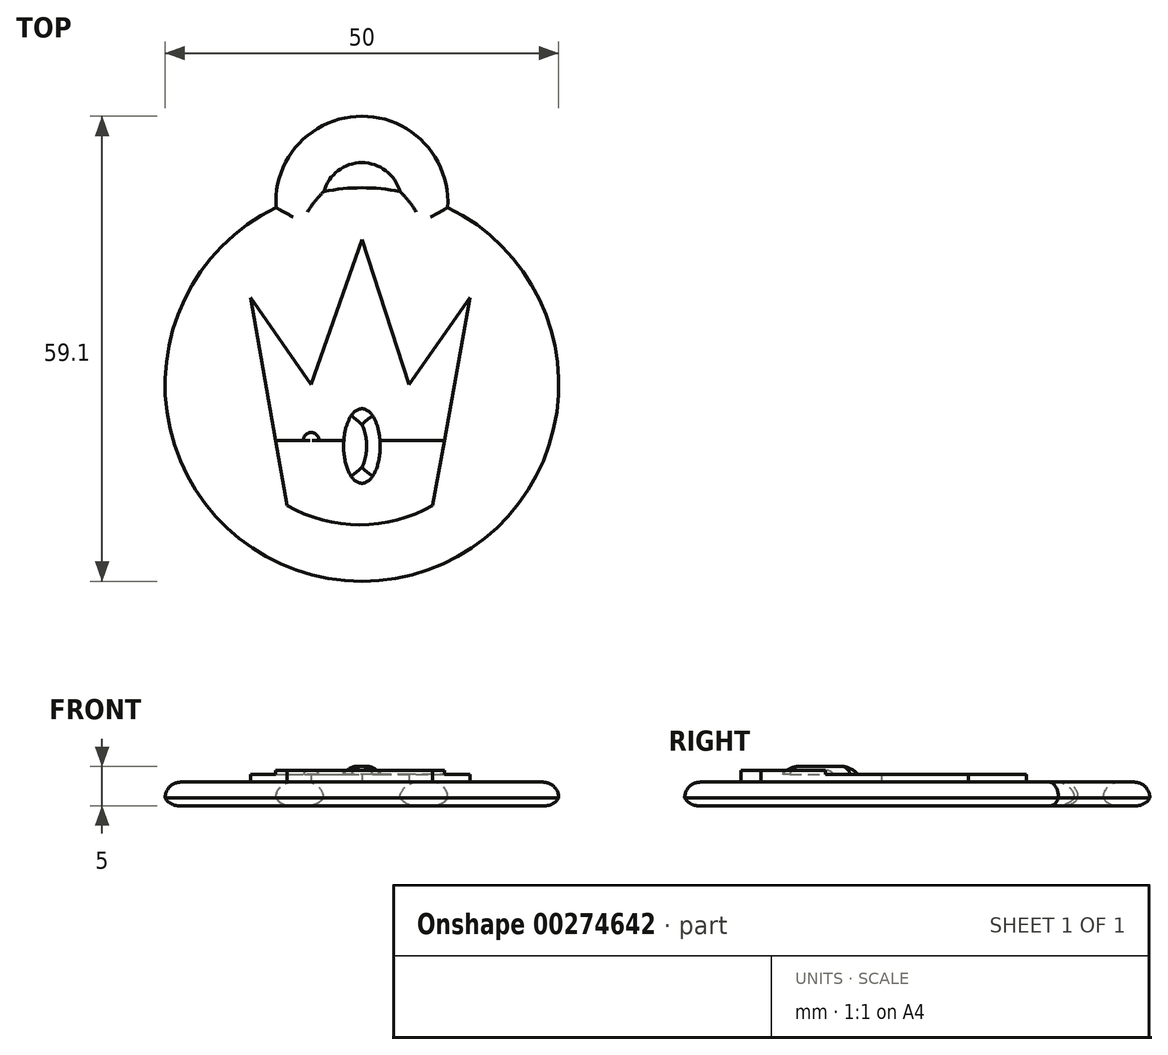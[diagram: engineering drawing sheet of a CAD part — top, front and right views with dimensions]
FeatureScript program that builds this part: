
annotation { "Feature Type Name" : "Feature", "Feature Type Description" : "" }
export const myFeature = defineFeature(function(context is Context, id is Id, definition is map)
    precondition{}
    {
        {
            var Q0;
            Q0=qCreatedBy(makeId("Top.planeOp"),FACE);
            var sketch = newSketch(context, id + "F0", { "sketchPlane" : qUnion([Q0])});
            skCircle(sketch, "E0", {"center": v(0, 0) * mm, "radius": 25 * mm});
            skSolve(sketch);
        }
        {
            var Q0;
            Q0=qCreatedBy(makeId("Top.planeOp"),FACE);
            var sketch = newSketch(context, id + "F1", { "sketchPlane" : qUnion([Q0])});
            skCircle(sketch, "E1", {"center": v(0, 23.17) * mm, "radius": 10.93 * mm});
            skCircle(sketch, "E2", {"center": v(0, 23.17) * mm, "radius": 5.01 * mm});
            skSolve(sketch);
        }
        {
            var Q0;
            Q0=makeQuery(id+"F0.imprint","IMPRINT",FACE,{"disambiguationData":[TD([[makeQuery(id+"F0.imprint","IMPRINT",EDGE,{"derivedFrom":sQuery(id+"F0.wireOp",EDGE,"E0")}),1.0]])]});
            var Q1;
            Q1=makeQuery(id+"F1.imprint","IMPRINT",FACE,{"disambiguationData":[TD([[makeQuery(id+"F1.imprint","IMPRINT",EDGE,{"derivedFrom":sQuery(id+"F1.wireOp",EDGE,"E1")}),1.0]])]});
            extrude(context, id + "F2", {"entities" : qUnion([Q0, Q1]), "depth" : 3 * mm});
        }
        {
            var Q0;
            Q0=makeQuery(id+"F2.opExtrude","CAP_FACE",FACE,{"disambiguationData":[OSD([sQuery(id+"F0.wireOp",EDGE,"E0")])],"isStart":false});
            var sketch = newSketch(context, id + "F3", { "sketchPlane" : qUnion([Q0])});
            skLineSegment(sketch, "E3", {"start": v(0, 18.31) * mm, "end": v(0, -16.1) * mm});
            skLineSegment(sketch, "E4", {"start": v(-13.94, 11.03) * mm, "end": v(13.74, 11.03) * mm});
            skSolve(sketch);
        }
        {
            var Q0;
            Q0=makeQuery(id+"F3.imprint","IMPRINT",FACE,{"disambiguationData":[TD([[makeQuery(id+"F3.imprint","IMPRINT",EDGE,{"derivedFrom":makeQuery(id+"F2.opExtrude","CAP_EDGE",EDGE,{"disambiguationData":[OSD([sQuery(id+"F0.wireOp",EDGE,"E0")])],"isStart":false})}),1.0]])]});
            var sketch = newSketch(context, id + "F4", { "sketchPlane" : qUnion([Q0])});
            skLineSegment(sketch, "E5", {"start": v(-14.16, 11.03) * mm, "end": v(-9.53, -15.33) * mm});
            skLineSegment(sketch, "E6", {"start": v(13.74, 11.03) * mm, "end": v(9, -15.33) * mm});
            skLineSegment(sketch, "E7", {"start": v(-14.16, 11.03) * mm, "end": v(-6.44, 0) * mm});
            skLineSegment(sketch, "E8", {"start": v(13.74, 11.03) * mm, "end": v(6.02, 0) * mm});
            skLineSegment(sketch, "E9", {"start": v(-6.44, 0) * mm, "end": v(0, 18.42) * mm});
            skLineSegment(sketch, "E10", {"start": v(6.02, 0) * mm, "end": v(0, 18.42) * mm});
            skArc(sketch, "E11", {"start": v(-9.53, -15.33) * mm, "mid": v(-0.27, -17.83) * mm, "end": v(9, -15.33) * mm});
            skSolve(sketch);
        }
        {
            var Q0;
            Q0 = qSketchRegion(id + "F4", true);
            extrude(context, id + "F5", {"entities" : qUnion([Q0]), "depth" : 1 * mm});
        }
        {
            var Q0;
            Q0=makeQuery(id+"F5.opExtrude","CAP_FACE",FACE,{"disambiguationData":[OSD([sQuery(id+"F4.wireOp",EDGE,"E5"),sQuery(id+"F4.wireOp",EDGE,"E6"),sQuery(id+"F4.wireOp",EDGE,"E7"),sQuery(id+"F4.wireOp",EDGE,"E8"),sQuery(id+"F4.wireOp",EDGE,"E9"),sQuery(id+"F4.wireOp",EDGE,"E10"),sQuery(id+"F4.wireOp",EDGE,"E11")])],"isStart":false});
            var sketch = newSketch(context, id + "F6", { "sketchPlane" : qUnion([Q0])});
            skEllipse(sketch, "E12", {"center": v(0, -7.8) * mm, "majorRadius": 4.74 * mm, "minorRadius": 2.32 * mm, "majorAxis": v(0, -1)});
            skSolve(sketch);
        }
        {
            var Q0;
            Q0=makeQuery(id+"F6.imprint","IMPRINT",FACE,{"disambiguationData":[TD([[makeQuery(id+"F6.imprint","IMPRINT",EDGE,{"derivedFrom":sQuery(id+"F6.wireOp",EDGE,"E12")}),1.0]])]});
            extrude(context, id + "F7", {"entities" : qUnion([Q0]), "operationType" : NewBodyOperationType.ADD, "depth" : 1 * mm});
        }
        {
            var Q0;
            Q0=makeQuery(id+"F7.opExtrude","CAP_EDGE",EDGE,{"disambiguationData":[OSD([sQuery(id+"F6.wireOp",EDGE,"E12")])],"isStart":false});
            fillet(context, id + "F8", {"entities" : qUnion([Q0]), "radius" : 2 * mm, "tangentPropagation" : true, "allowEdgeOverflow" : false});
        }
        {
            var Q0;
            Q0=makeQuery(id+"F2.opExtrude","SWEPT_BODY",BODY,{"disambiguationData":[OSD([sQuery(id+"F0.wireOp",EDGE,"E0")])]});
            var Q1;
            Q1=makeQuery(id+"F2.opExtrude","SWEPT_BODY",BODY,{"disambiguationData":[OSD([sQuery(id+"F1.wireOp",EDGE,"E1"),sQuery(id+"F1.wireOp",EDGE,"E2")])]});
            var Q2;
            Q2=makeQuery(id+"F5.opExtrude","SWEPT_BODY",BODY,{"disambiguationData":[OSD([sQuery(id+"F4.wireOp",EDGE,"E5"),sQuery(id+"F4.wireOp",EDGE,"E6"),sQuery(id+"F4.wireOp",EDGE,"E7"),sQuery(id+"F4.wireOp",EDGE,"E8"),sQuery(id+"F4.wireOp",EDGE,"E9"),sQuery(id+"F4.wireOp",EDGE,"E10"),sQuery(id+"F4.wireOp",EDGE,"E11")])]});
            booleanBodies(context, id + "F9", {"operationType" : BooleanOperationType.UNION, "tools" : qUnion([Q0, Q1, Q2])});
        }
        {
            var Q0;
            {var subQ0=sQuery(id+"F0.wireOp",EDGE,"E0");var subQ1=sQuery(id+"F1.wireOp",EDGE,"E1");Q0=makeQuery(id+"F9.opBoolean","SPLIT",EDGE,{"disambiguationData":[TD([makeQuery(id+"F2.opExtrude","SWEPT_FACE",FACE,{"disambiguationData":[OSD([subQ1])]})])],"derivedFrom":makeQuery(id+"F2.opExtrude","CAP_EDGE",EDGE,{"disambiguationData":[OSD([subQ0])],"isStart":false})});}
            var Q1;
            Q1=makeQuery(id+"F2.opExtrude","CAP_EDGE",EDGE,{"disambiguationData":[OSD([sQuery(id+"F1.wireOp",EDGE,"E1")])],"isStart":false});
            var Q2;
            {var subQ0=sQuery(id+"F0.wireOp",EDGE,"E0");var subQ1=sQuery(id+"F1.wireOp",EDGE,"E2");Q2=makeQuery(id+"F9.opBoolean","SPLIT",EDGE,{"disambiguationData":[TD([makeQuery(id+"F2.opExtrude","SWEPT_FACE",FACE,{"disambiguationData":[OSD([subQ1])]})])],"derivedFrom":makeQuery(id+"F2.opExtrude","CAP_EDGE",EDGE,{"disambiguationData":[OSD([subQ0])],"isStart":false})});}
            var Q3;
            Q3=makeQuery(id+"F2.opExtrude","CAP_EDGE",EDGE,{"disambiguationData":[OSD([sQuery(id+"F1.wireOp",EDGE,"E2")])],"isStart":false});
            fillet(context, id + "F10", {"entities" : qUnion([Q0, Q1, Q2, Q3]), "radius" : 2 * mm, "tangentPropagation" : true, "allowEdgeOverflow" : false});
        }
        {
            var Q0;
            {var subQ0=sQuery(id+"F0.wireOp",EDGE,"E0");var subQ1=sQuery(id+"F1.wireOp",EDGE,"E1");Q0=makeQuery(id+"F9.opBoolean","SPLIT",EDGE,{"disambiguationData":[TD([makeQuery(id+"F2.opExtrude","SWEPT_FACE",FACE,{"disambiguationData":[OSD([subQ1])]})])],"derivedFrom":makeQuery(id+"F2.opExtrude","CAP_EDGE",EDGE,{"disambiguationData":[OSD([subQ0])],"isStart":true})});}
            var Q1;
            Q1=makeQuery(id+"F2.opExtrude","CAP_EDGE",EDGE,{"disambiguationData":[OSD([sQuery(id+"F1.wireOp",EDGE,"E1")])],"isStart":true});
            var Q2;
            {var subQ0=sQuery(id+"F0.wireOp",EDGE,"E0");var subQ1=sQuery(id+"F1.wireOp",EDGE,"E2");Q2=makeQuery(id+"F9.opBoolean","SPLIT",EDGE,{"disambiguationData":[TD([makeQuery(id+"F2.opExtrude","SWEPT_FACE",FACE,{"disambiguationData":[OSD([subQ1])]})])],"derivedFrom":makeQuery(id+"F2.opExtrude","CAP_EDGE",EDGE,{"disambiguationData":[OSD([subQ0])],"isStart":true})});}
            var Q3;
            Q3=makeQuery(id+"F2.opExtrude","CAP_EDGE",EDGE,{"disambiguationData":[OSD([sQuery(id+"F1.wireOp",EDGE,"E2")])],"isStart":true});
            fillet(context, id + "F11", {"entities" : qUnion([Q0, Q1, Q2, Q3]), "radius" : 2 * mm, "tangentPropagation" : true, "allowEdgeOverflow" : false});
        }
        {
            var Q0;
            Q0=makeQuery(id+"F5.opExtrude","CAP_FACE",FACE,{"disambiguationData":[OSD([sQuery(id+"F4.wireOp",EDGE,"E5"),sQuery(id+"F4.wireOp",EDGE,"E6"),sQuery(id+"F4.wireOp",EDGE,"E7"),sQuery(id+"F4.wireOp",EDGE,"E8"),sQuery(id+"F4.wireOp",EDGE,"E9"),sQuery(id+"F4.wireOp",EDGE,"E10"),sQuery(id+"F4.wireOp",EDGE,"E11")])],"isStart":false});
            var sketch = newSketch(context, id + "F12", { "sketchPlane" : qUnion([Q0])});
            skLineSegment(sketch, "E13", {"start": v(6.02, 0) * mm, "end": v(6.02, -16.72) * mm});
            skLineSegment(sketch, "E14", {"start": v(-6.44, 0) * mm, "end": v(-6.44, -16.72) * mm});
            skLineSegment(sketch, "E15", {"start": v(-10.98, -7.1) * mm, "end": v(10.48, -7.1) * mm});
            skCircle(sketch, "E16", {"center": v(-6.44, -7.1) * mm, "radius": 1 * mm});
            skCircle(sketch, "E17", {"center": v(6.02, -7.1) * mm, "radius": 1 * mm});
            skSolve(sketch);
        }
        {
            var Q0;
            {var subQ0=sQuery(id+"F12.wireOp",EDGE,"E16");var subQ1=sQuery(id+"F12.wireOp",EDGE,"E14");var subQ2=makeQuery(id+"F12.imprint","INTERSECT",VERTEX,{"disambiguationData":[OD(1.0)],"derivedFrom":[subQ1,subQ0]});Q0=makeQuery(id+"F12.imprint","IMPRINT",FACE,{"disambiguationData":[TD([[makeQuery(id+"F12.imprint","IMPRINT",EDGE,{"disambiguationData":[TD([[subQ2,-1.0]])],"derivedFrom":subQ1}),1.0]])]});}
            var Q1;
            {var subQ0=sQuery(id+"F12.wireOp",EDGE,"E16");var subQ1=sQuery(id+"F12.wireOp",EDGE,"E14");var subQ2=makeQuery(id+"F12.imprint","INTERSECT",VERTEX,{"disambiguationData":[OD(1.0)],"derivedFrom":[subQ1,subQ0]});Q1=makeQuery(id+"F12.imprint","IMPRINT",FACE,{"disambiguationData":[TD([[makeQuery(id+"F12.imprint","IMPRINT",EDGE,{"disambiguationData":[TD([[subQ2,-1.0]])],"derivedFrom":subQ1}),-1.0]])]});}
            var Q2;
            {var subQ0=sQuery(id+"F12.wireOp",EDGE,"E16");var subQ1=sQuery(id+"F12.wireOp",EDGE,"E14");var subQ2=makeQuery(id+"F12.imprint","INTERSECT",VERTEX,{"disambiguationData":[OD(0.0)],"derivedFrom":[subQ1,subQ0]});Q2=makeQuery(id+"F12.imprint","IMPRINT",FACE,{"disambiguationData":[TD([[makeQuery(id+"F12.imprint","IMPRINT",EDGE,{"disambiguationData":[TD([[subQ2,1.0]])],"derivedFrom":subQ1}),-1.0]])]});}
            var Q3;
            {var subQ0=sQuery(id+"F12.wireOp",EDGE,"E16");var subQ1=sQuery(id+"F12.wireOp",EDGE,"E14");var subQ2=makeQuery(id+"F12.imprint","INTERSECT",VERTEX,{"disambiguationData":[OD(0.0)],"derivedFrom":[subQ1,subQ0]});Q3=makeQuery(id+"F12.imprint","IMPRINT",FACE,{"disambiguationData":[TD([[makeQuery(id+"F12.imprint","IMPRINT",EDGE,{"disambiguationData":[TD([[subQ2,1.0]])],"derivedFrom":subQ1}),1.0]])]});}
            var Q4;
            {var subQ0=sQuery(id+"F12.wireOp",EDGE,"E17");var subQ1=sQuery(id+"F12.wireOp",EDGE,"E13");var subQ2=makeQuery(id+"F12.imprint","INTERSECT",VERTEX,{"disambiguationData":[OD(0.0)],"derivedFrom":[subQ1,subQ0]});Q4=makeQuery(id+"F12.imprint","IMPRINT",FACE,{"disambiguationData":[TD([[makeQuery(id+"F12.imprint","IMPRINT",EDGE,{"disambiguationData":[TD([[subQ2,-1.0]])],"derivedFrom":subQ1}),1.0]])]});}
            var Q5;
            {var subQ0=sQuery(id+"F12.wireOp",EDGE,"E17");var subQ1=sQuery(id+"F12.wireOp",EDGE,"E13");var subQ2=makeQuery(id+"F12.imprint","INTERSECT",VERTEX,{"disambiguationData":[OD(0.0)],"derivedFrom":[subQ1,subQ0]});Q5=makeQuery(id+"F12.imprint","IMPRINT",FACE,{"disambiguationData":[TD([[makeQuery(id+"F12.imprint","IMPRINT",EDGE,{"disambiguationData":[TD([[subQ2,-1.0]])],"derivedFrom":subQ1}),-1.0]])]});}
            var Q6;
            {var subQ0=sQuery(id+"F12.wireOp",EDGE,"E15");var subQ1=sQuery(id+"F12.wireOp",EDGE,"E13");var subQ2=makeQuery(id+"F12.imprint","INTERSECT",VERTEX,{"derivedFrom":[subQ1,subQ0]});Q6=makeQuery(id+"F12.imprint","IMPRINT",FACE,{"disambiguationData":[TD([[makeQuery(id+"F12.imprint","IMPRINT",EDGE,{"disambiguationData":[TD([[subQ2,-1.0]])],"derivedFrom":subQ1}),-1.0]])]});}
            var Q7;
            {var subQ0=sQuery(id+"F12.wireOp",EDGE,"E15");var subQ1=sQuery(id+"F12.wireOp",EDGE,"E13");var subQ2=makeQuery(id+"F12.imprint","INTERSECT",VERTEX,{"derivedFrom":[subQ1,subQ0]});Q7=makeQuery(id+"F12.imprint","IMPRINT",FACE,{"disambiguationData":[TD([[makeQuery(id+"F12.imprint","IMPRINT",EDGE,{"disambiguationData":[TD([[subQ2,-1.0]])],"derivedFrom":subQ1}),1.0]])]});}
            extrude(context, id + "F13", {"entities" : qUnion([Q0, Q1, Q2, Q3, Q4, Q5, Q6, Q7]), "operationType" : NewBodyOperationType.ADD, "depth" : 0.5 * mm});
        }
        {
            var Q0;
            Q0=makeQuery(id+"F13.opExtrude","CAP_EDGE",EDGE,{"disambiguationData":[OSD([sQuery(id+"F12.wireOp",EDGE,"E16")])],"isStart":false});
            var Q1;
            Q1=makeQuery(id+"F13.opExtrude","CAP_EDGE",EDGE,{"disambiguationData":[OSD([sQuery(id+"F12.wireOp",EDGE,"E17")])],"isStart":false});
            fillet(context, id + "F14", {"entities" : qUnion([Q0, Q1]), "radius" : 1 * mm, "tangentPropagation" : true, "allowEdgeOverflow" : false});
        }
    });
